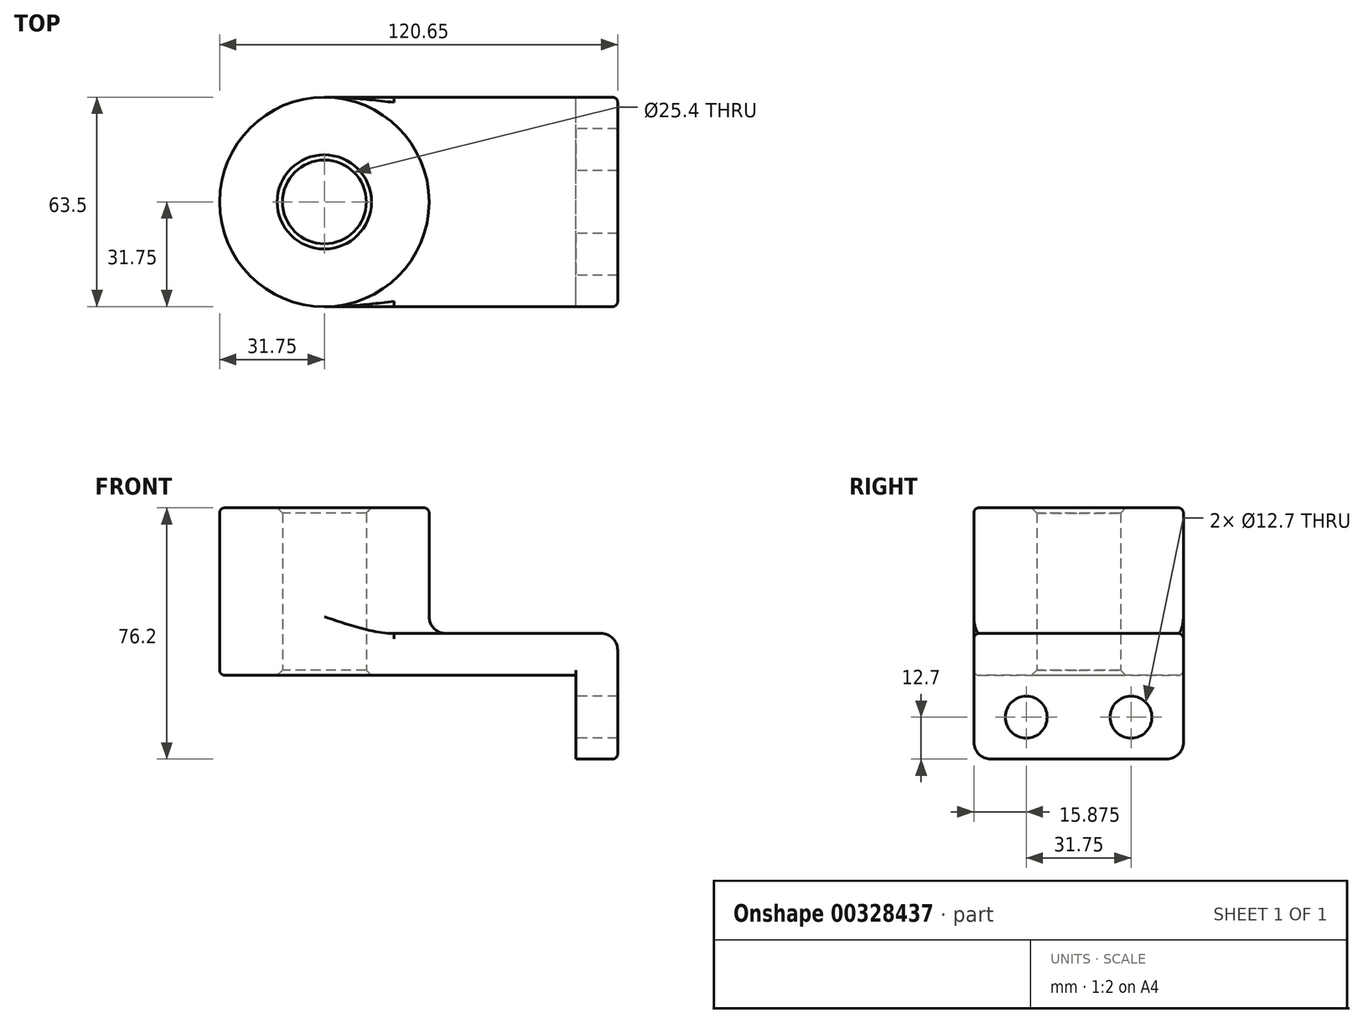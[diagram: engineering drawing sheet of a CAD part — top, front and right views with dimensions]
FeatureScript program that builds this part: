
annotation { "Feature Type Name" : "Feature", "Feature Type Description" : "" }
export const myFeature = defineFeature(function(context is Context, id is Id, definition is map)
    precondition{}
    {
        {
            var Q0;
            Q0=qCreatedBy(makeId("Top.planeOp"),FACE);
            var sketch = newSketch(context, id + "F0", { "sketchPlane" : qUnion([Q0])});
            skLineSegment(sketch, "E0.bottom", {"start": v(38.1, -31.75) * mm, "end": v(-38.1, -31.75) * mm});
            skLineSegment(sketch, "E0.top", {"start": v(38.1, 31.75) * mm, "end": v(-38.1, 31.75) * mm});
            skLineSegment(sketch, "E0.left", {"start": v(38.1, -31.75) * mm, "end": v(38.1, 31.75) * mm});
            skLineSegment(sketch, "E0.right", {"start": v(-38.1, -31.75) * mm, "end": v(-38.1, 31.75) * mm});
            skPoint(sketch, "E0.middle", {"position": v(0, 0) * mm});
            skCircle(sketch, "E1", {"center": v(-38.1, 0) * mm, "radius": 31.75 * mm});
            skCircle(sketch, "E2", {"center": v(-38.1, 0) * mm, "radius": 12.7 * mm});
            skSolve(sketch);
        }
        {
            var Q0;
            {var subQ1=sQuery(id+"F0.wireOp",EDGE,"E0.right");var subQ3=sQuery(id+"F0.wireOp",EDGE,"E2");var subQ4=makeQuery(id+"F0.imprint","INTERSECT",VERTEX,{"disambiguationData":[OD(0.0)],"derivedFrom":[subQ1,subQ3]});Q0=makeQuery(id+"F0.imprint","IMPRINT",FACE,{"disambiguationData":[TD([[makeQuery(id+"F0.imprint","IMPRINT",EDGE,{"disambiguationData":[TD([[subQ4,-1.0]])],"derivedFrom":subQ3}),-1.0]])]});}
            var Q1;
            {var subQ1=sQuery(id+"F0.wireOp",EDGE,"E0.right");var subQ3=sQuery(id+"F0.wireOp",EDGE,"E2");var subQ4=makeQuery(id+"F0.imprint","INTERSECT",VERTEX,{"disambiguationData":[OD(0.0)],"derivedFrom":[subQ1,subQ3]});Q1=makeQuery(id+"F0.imprint","IMPRINT",FACE,{"disambiguationData":[TD([[makeQuery(id+"F0.imprint","IMPRINT",EDGE,{"disambiguationData":[TD([[subQ4,1.0]])],"derivedFrom":subQ3}),-1.0]])]});}
            var Q2;
            {var subQ0=sQuery(id+"F0.wireOp",EDGE,"E0.bottom");Q2=makeQuery(id+"F0.imprint","IMPRINT",FACE,{"disambiguationData":[TD([[makeQuery(id+"F0.imprint","IMPRINT",EDGE,{"derivedFrom":subQ0}),-1.0]])]});}
            extrude(context, id + "F1", {"entities" : qUnion([Q0, Q1, Q2]), "depth" : 12.7 * mm});
        }
        {
            var Q0;
            {var subQ1=sQuery(id+"F0.wireOp",EDGE,"E0.right");var subQ3=sQuery(id+"F0.wireOp",EDGE,"E2");var subQ4=makeQuery(id+"F0.imprint","INTERSECT",VERTEX,{"disambiguationData":[OD(0.0)],"derivedFrom":[subQ1,subQ3]});Q0=makeQuery(id+"F0.imprint","IMPRINT",FACE,{"disambiguationData":[TD([[makeQuery(id+"F0.imprint","IMPRINT",EDGE,{"disambiguationData":[TD([[subQ4,1.0]])],"derivedFrom":subQ3}),-1.0]])]});}
            var Q1;
            {var subQ1=sQuery(id+"F0.wireOp",EDGE,"E0.right");var subQ3=sQuery(id+"F0.wireOp",EDGE,"E2");var subQ4=makeQuery(id+"F0.imprint","INTERSECT",VERTEX,{"disambiguationData":[OD(0.0)],"derivedFrom":[subQ1,subQ3]});Q1=makeQuery(id+"F0.imprint","IMPRINT",FACE,{"disambiguationData":[TD([[makeQuery(id+"F0.imprint","IMPRINT",EDGE,{"disambiguationData":[TD([[subQ4,-1.0]])],"derivedFrom":subQ3}),-1.0]])]});}
            extrude(context, id + "F2", {"entities" : qUnion([Q0, Q1]), "operationType" : NewBodyOperationType.ADD, "depth" : 50.8 * mm});
        }
        {
            var Q0;
            Q0=makeQuery(id+"F1.opExtrude","SWEPT_FACE",FACE,{"disambiguationData":[OSD([sQuery(id+"F0.wireOp",EDGE,"E0.left")])]});
            var sketch = newSketch(context, id + "F3", { "sketchPlane" : qUnion([Q0])});
            skLineSegment(sketch, "E3.bottom", {"start": v(-31.75, 12.7) * mm, "end": v(31.75, 12.7) * mm});
            skLineSegment(sketch, "E3.top", {"start": v(-31.75, -25.4) * mm, "end": v(31.75, -25.4) * mm});
            skLineSegment(sketch, "E3.left", {"start": v(-31.75, 12.7) * mm, "end": v(-31.75, -25.4) * mm});
            skLineSegment(sketch, "E3.right", {"start": v(31.75, 12.7) * mm, "end": v(31.75, -25.4) * mm});
            skLineSegment(sketch, "E4", {"start": v(0, 0) * mm, "end": v(0, -25.4) * mm});
            skCircle(sketch, "E5", {"center": v(-15.87, -12.7) * mm, "radius": 6.35 * mm});
            skCircle(sketch, "E6.MirrorC", {"center": v(15.87, -12.7) * mm, "radius": 6.35 * mm});
            skSolve(sketch);
        }
        {
            var Q0;
            Q0 = qSketchRegion(id + "F3", true);
            extrude(context, id + "F4", {"entities" : qUnion([Q0]), "operationType" : NewBodyOperationType.ADD, "depth" : 12.7 * mm});
        }
        {
            var Q0;
            {var subQ0=sQuery(id+"F0.wireOp",EDGE,"E1");Q0=makeQuery(id+"F2.boolean.opBoolean","INTERSECT",EDGE,{"derivedFrom":[makeQuery(id+"F1.opExtrude","CAP_FACE",FACE,{"disambiguationData":[OSD([sQuery(id+"F0.wireOp",EDGE,"E0.bottom"),sQuery(id+"F0.wireOp",EDGE,"E0.top"),sQuery(id+"F0.wireOp",EDGE,"E0.left"),subQ0,sQuery(id+"F0.wireOp",EDGE,"E2")])],"isStart":false}),makeQuery(id+"F2.opExtrude","SWEPT_FACE",FACE,{"disambiguationData":[OSD([subQ0])]})]});}
            var Q1;
            Q1=makeQuery(id+"F4.opExtrude","SWEPT_EDGE",EDGE,{"disambiguationData":[OSD([sQuery(id+"F3.wireOp",EDGE,"E3.top"),sQuery(id+"F3.wireOp",EDGE,"E3.left")])]});
            var Q2;
            Q2=makeQuery(id+"F4.opExtrude","SWEPT_EDGE",EDGE,{"disambiguationData":[OSD([sQuery(id+"F3.wireOp",EDGE,"E3.top"),sQuery(id+"F3.wireOp",EDGE,"E3.right")])]});
            var Q3;
            Q3=makeQuery(id+"F4.opExtrude","CAP_EDGE",EDGE,{"disambiguationData":[OSD([sQuery(id+"F3.wireOp",EDGE,"E3.bottom")])],"isStart":false});
            var Q4;
            Q4=makeQuery(id+"F1.opExtrude","CAP_EDGE",EDGE,{"disambiguationData":[OSD([sQuery(id+"F0.wireOp",EDGE,"E0.left")])],"isStart":true});
            fillet(context, id + "F5", {"entities" : qUnion([Q0, Q1, Q2, Q3, Q4]), "radius" : 5.08 * mm, "tangentPropagation" : true, "allowEdgeOverflow" : false});
        }
        {
            var Q0;
            Q0=makeQuery(id+"F4.boolean.opBoolean","MERGE",EDGE,{"derivedFrom":[makeQuery(id+"F1.opExtrude","CAP_EDGE",EDGE,{"disambiguationData":[OSD([sQuery(id+"F0.wireOp",EDGE,"E0.top")])],"isStart":false}),makeQuery(id+"F4.opExtrude","SWEPT_EDGE",EDGE,{"disambiguationData":[OSD([sQuery(id+"F3.wireOp",EDGE,"E3.bottom"),sQuery(id+"F3.wireOp",EDGE,"E3.right")])]})]});
            var Q1;
            Q1=makeQuery(id+"F4.boolean.opBoolean","MERGE",EDGE,{"derivedFrom":[makeQuery(id+"F1.opExtrude","CAP_EDGE",EDGE,{"disambiguationData":[OSD([sQuery(id+"F0.wireOp",EDGE,"E0.bottom")])],"isStart":false}),makeQuery(id+"F4.opExtrude","SWEPT_EDGE",EDGE,{"disambiguationData":[OSD([sQuery(id+"F3.wireOp",EDGE,"E3.bottom"),sQuery(id+"F3.wireOp",EDGE,"E3.left")])]})]});
            var Q2;
            Q2=makeQuery(id+"F1.opExtrude","CAP_EDGE",EDGE,{"disambiguationData":[OSD([sQuery(id+"F0.wireOp",EDGE,"E0.top")])],"isStart":true});
            var Q3;
            Q3=makeQuery(id+"F2.opExtrude","CAP_EDGE",EDGE,{"disambiguationData":[OSD([sQuery(id+"F0.wireOp",EDGE,"E1")])],"isStart":false});
            fillet(context, id + "F6", {"entities" : qUnion([Q0, Q1, Q2, Q3]), "radius" : 1.59 * mm, "tangentPropagation" : true, "allowEdgeOverflow" : false});
        }
        {
            var Q0;
            {var subQ0=sQuery(id+"F0.wireOp",EDGE,"E2");Q0=makeQuery(id+"F2.boolean.opBoolean","MERGE",FACE,{"derivedFrom":[makeQuery(id+"F1.opExtrude","SWEPT_FACE",FACE,{"disambiguationData":[OSD([subQ0])]}),makeQuery(id+"F2.opExtrude","SWEPT_FACE",FACE,{"disambiguationData":[OSD([subQ0])]})]});}
            chamfer(context, id + "F7", {"entities" : qUnion([Q0]), "width" : 1.59 * mm, "tangentPropagation" : true});
        }
    });
